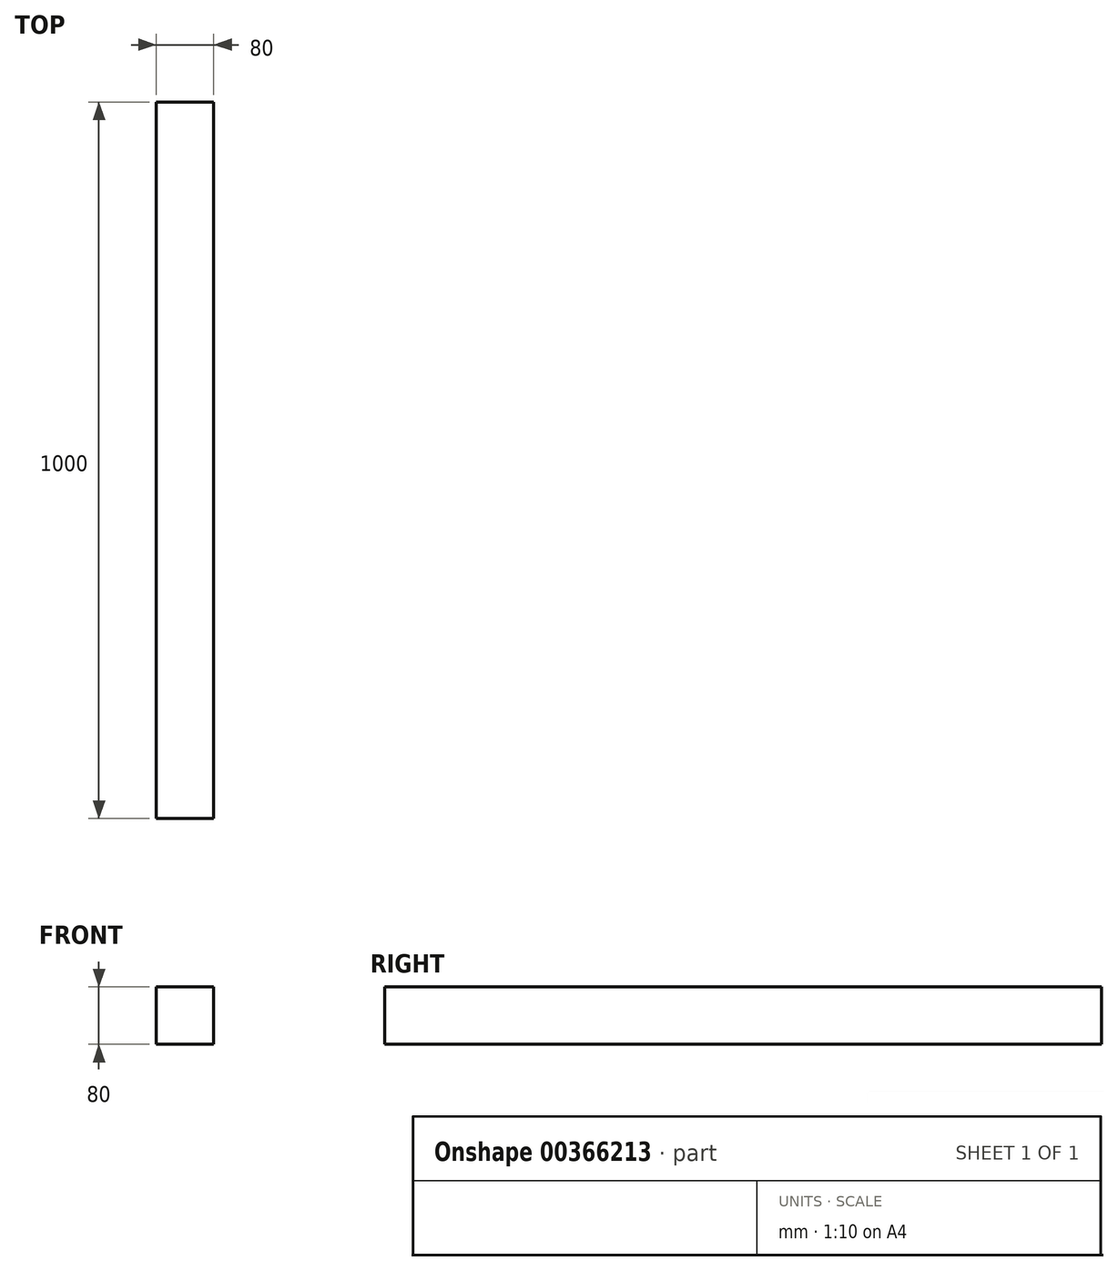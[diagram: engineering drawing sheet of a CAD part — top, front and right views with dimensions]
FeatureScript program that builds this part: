
annotation { "Feature Type Name" : "Feature", "Feature Type Description" : "" }
export const myFeature = defineFeature(function(context is Context, id is Id, definition is map)
    precondition{}
    {
        {
            var Q0;
            Q0=qCreatedBy(makeId("Front.planeOp"),FACE);
            var sketch = newSketch(context, id + "F0", { "sketchPlane" : qUnion([Q0])});
            skLineSegment(sketch, "E0.bottom", {"start": v(87.5, 78.9) * mm, "end": v(7.5, 78.9) * mm});
            skLineSegment(sketch, "E0.top", {"start": v(87.5, -1.1) * mm, "end": v(7.5, -1.1) * mm});
            skLineSegment(sketch, "E0.left", {"start": v(87.5, 78.9) * mm, "end": v(87.5, -1.1) * mm});
            skLineSegment(sketch, "E0.right", {"start": v(7.5, 78.9) * mm, "end": v(7.5, -1.1) * mm});
            skSolve(sketch);
        }
        {
            var Q0;
            Q0 = qSketchRegion(id + "F0", true);
            extrude(context, id + "F1", {"entities" : qUnion([Q0]), "depth" : 1000 * mm});
        }
        {
            var Q0;
            Q0 = qSketchRegion(id + "F0", true);
            extrude(context, id + "F2", {"entities" : qUnion([Q0]), "operationType" : NewBodyOperationType.ADD, "depth" : 1000 * mm});
        }
    });
